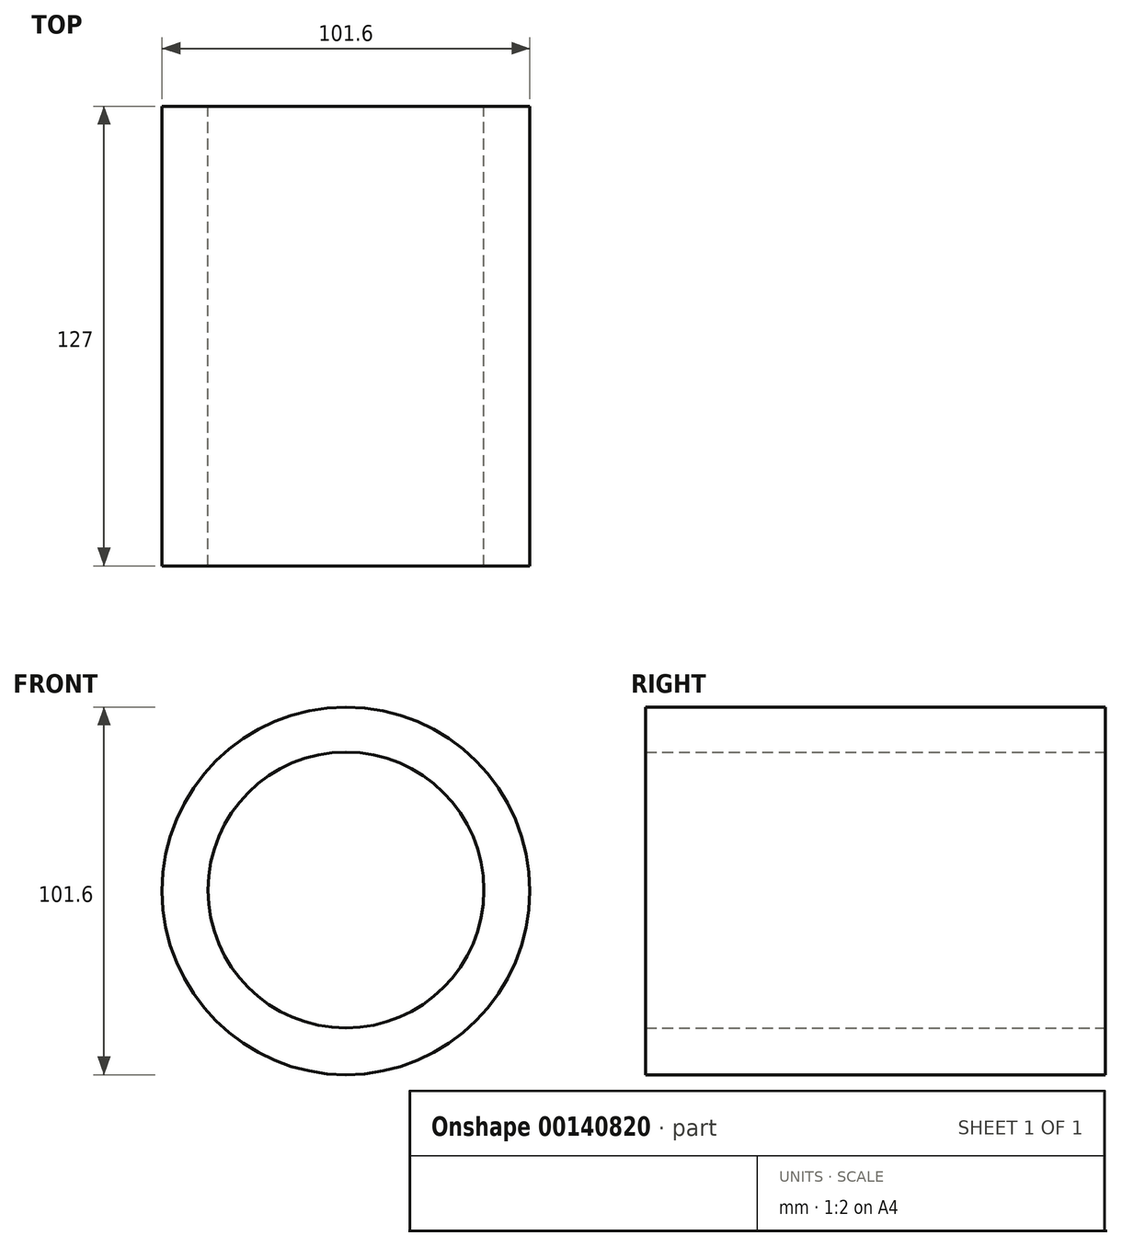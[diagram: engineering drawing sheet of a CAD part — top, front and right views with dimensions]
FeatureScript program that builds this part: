
annotation { "Feature Type Name" : "Feature", "Feature Type Description" : "" }
export const myFeature = defineFeature(function(context is Context, id is Id, definition is map)
    precondition{}
    {
        {
            var Q0;
            Q0=qCreatedBy(makeId("Front.planeOp"),FACE);
            var sketch = newSketch(context, id + "F0", { "sketchPlane" : qUnion([Q0])});
            skCircle(sketch, "E0", {"center": v(0, 0) * mm, "radius": 50.8 * mm});
            skCircle(sketch, "E1", {"center": v(0, 0.22) * mm, "radius": 38.1 * mm});
            skSolve(sketch);
        }
        {
            var Q0;
            Q0=makeQuery(id+"F0.imprint","IMPRINT",FACE,{"disambiguationData":[TD([[makeQuery(id+"F0.imprint","IMPRINT",EDGE,{"derivedFrom":sQuery(id+"F0.wireOp",EDGE,"E0")}),1.0]])]});
            extrude(context, id + "F1", {"entities" : qUnion([Q0]), "endBound" : BoundingType.SYMMETRIC, "depth" : 127 * mm});
        }
    });
